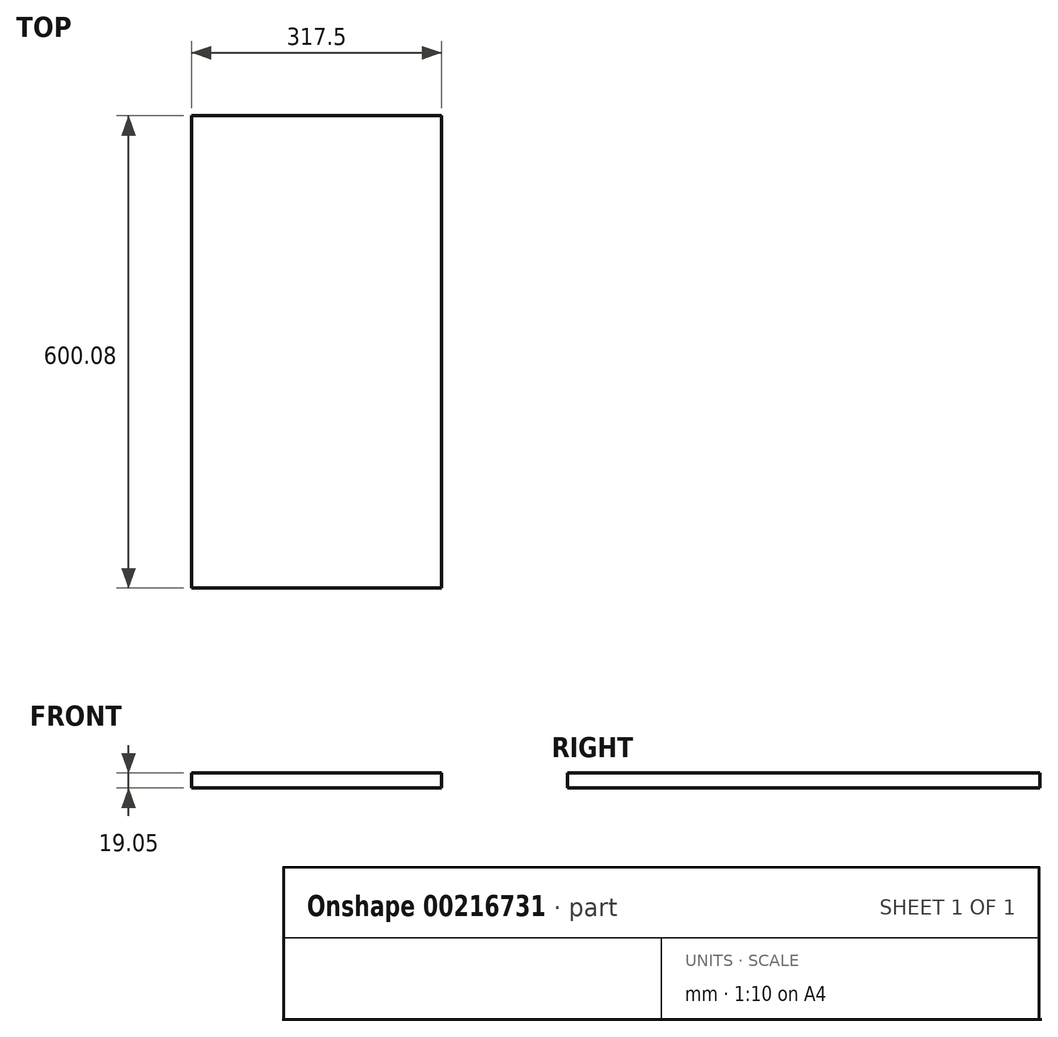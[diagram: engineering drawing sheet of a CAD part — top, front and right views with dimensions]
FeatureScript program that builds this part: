
annotation { "Feature Type Name" : "Feature", "Feature Type Description" : "" }
export const myFeature = defineFeature(function(context is Context, id is Id, definition is map)
    precondition{}
    {
        {
            var Q0;
            Q0=qCreatedBy(makeId("Top.planeOp"),FACE);
            var sketch = newSketch(context, id + "F0", { "sketchPlane" : qUnion([Q0])});
            skLineSegment(sketch, "E0.bottom", {"start": v(0, 0) * mm, "end": v(317.5, 0) * mm});
            skLineSegment(sketch, "E0.top", {"start": v(0, 600.07) * mm, "end": v(317.5, 600.07) * mm});
            skLineSegment(sketch, "E0.left", {"start": v(0, 0) * mm, "end": v(0, 600.07) * mm});
            skLineSegment(sketch, "E0.right", {"start": v(317.5, 0) * mm, "end": v(317.5, 600.07) * mm});
            skSolve(sketch);
        }
        {
            var Q0;
            Q0 = qSketchRegion(id + "F0", true);
            extrude(context, id + "F1", {"entities" : qUnion([Q0]), "depth" : 19.05 * mm});
        }
    });
